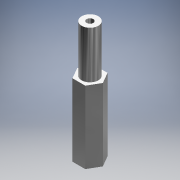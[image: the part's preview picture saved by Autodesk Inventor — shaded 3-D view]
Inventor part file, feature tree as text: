
AUTODESK INVENTOR PART (.ipt)
format: ipt  version: 2017 SP1 (Build 210196100, 196)  size: 118,272 bytes
history: native  units: in
note: dims shown in document units (in); Inventor stores cm internally (conversion verified against a paired STEP export)
features: extrude x4, sketch x4
ambient origin geometry x8: Origin, YZ Plane, XZ Plane, XY Plane, X Axis, Y Axis, Z Axis, Center Point
bodies: Solid1 (feature_tree)
feature tree (8):
  extrude  "Extrusion1"  Depth=1.625in TaperAngle=0.0deg
  extrude  "Extrusion2"  Depth=1.0625in TaperAngle=0.0deg
  extrude  "Extrusion3"  Depth=1.0in TaperAngle=0.0deg
  extrude  "Extrusion4"  [1 undecoded]
  sketch  "Sketch1"  dims[d0=0.5in d1=1.625in d2=0.0in]
  sketch  "Sketch2"  dims[d3=0.375in d4=1.0625in d5=0.0in]
  sketch  "Sketch3"  dims[d7=0.15in d8=1.0in d9=0.0in]
  sketch  "Sketch4"  dims[d10=1.0in d11=0.0in]
note: 1 required parameter value undecoded (feature->parameter linkage not recoverable at this tier; creation-order binding heuristic only, values carry confidence <= 0.55)
